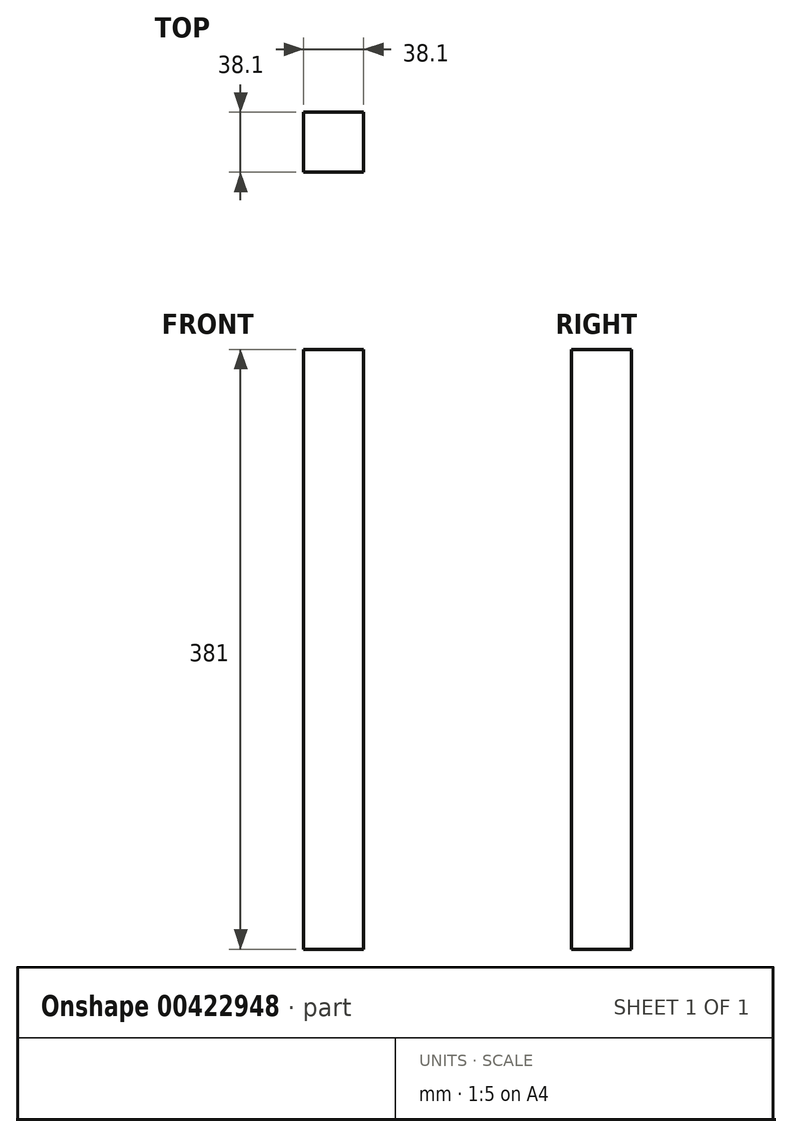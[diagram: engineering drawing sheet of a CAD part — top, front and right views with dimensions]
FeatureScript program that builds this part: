
annotation { "Feature Type Name" : "Feature", "Feature Type Description" : "" }
export const myFeature = defineFeature(function(context is Context, id is Id, definition is map)
    precondition{}
    {
        {
            var Q0;
            Q0=qCreatedBy(makeId("Top.planeOp"),FACE);
            var sketch = newSketch(context, id + "F0", { "sketchPlane" : qUnion([Q0])});
            skLineSegment(sketch, "E0.bottom", {"start": v(19.05, 19.05) * mm, "end": v(-19.05, 19.05) * mm});
            skLineSegment(sketch, "E0.top", {"start": v(19.05, -19.05) * mm, "end": v(-19.05, -19.05) * mm});
            skLineSegment(sketch, "E0.left", {"start": v(19.05, 19.05) * mm, "end": v(19.05, -19.05) * mm});
            skLineSegment(sketch, "E0.right", {"start": v(-19.05, 19.05) * mm, "end": v(-19.05, -19.05) * mm});
            skPoint(sketch, "E0.middle", {"position": v(0, 0) * mm});
            skSolve(sketch);
        }
        {
            var Q0;
            Q0=makeQuery(id+"F0.imprint","IMPRINT",FACE,{"disambiguationData":[TD([[makeQuery(id+"F0.imprint","IMPRINT",EDGE,{"derivedFrom":sQuery(id+"F0.wireOp",EDGE,"E0.bottom")}),1.0]])]});
            extrude(context, id + "F1", {"entities" : qUnion([Q0]), "depth" : 381 * mm, "offsetDistance" : 25.4 * mm});
        }
    });
